# Revit family: Cover_Access_Round-Zurn-Z1469
name_source: partatom
category: Plumbing Fixtures
units: mm (PartAtom-declared; Revit-internal decimal feet)

## family parameters
Cut with Voids When Loaded = No
Host = Face
Maintain Annotation Orientation = No
OmniClass Number = 23.60.30.11.14
OmniClass Title = Pipework Fittings
Part Type = Normal
Room Calculation Point = No
Round Connector Dimension = Use Radius
Shared = No

## types (10) — shared parameters
Assembly Code = D2030100
CW Connection = No
Default Elevation = 20 "
Description = ROUND ACCESS COVER
HW Connection = No
Manufacturer = Zurn Water, LLC
Manufacurer Brand = Zurn
Modified Date = 02/13/2026
Product Documentation Link = https://files.zurn.com
Product Page URL = https://www.zurn.com
Product data url = https://www.bimobject.com
URL = www.zurn.com
Vent Connection = No
WFU = 1
Waste Connection = Yes
zero-valued in all types: CWFU, HWFU

## per-type parameters (varying)
| type | Approx. Weight (Lbs) | Cover Dia (A) | Main Material | Model | Type Comments |
| ZS1469 4 Inch | 1 " | 4 " | Steel – Zurn – Stainless – Polished | ZS1469 | ZS1469-4 Inch Cover |
| ZS1469 5 Inch | 1 " | 5 " | Steel – Zurn – Stainless – Polished | ZS1469 | ZS1469-5 Inch Cover |
| ZS1469 7 Inch | 2 " | 7 " | Steel – Zurn – Stainless – Polished | ZS1469 | ZS1469-7 Inch Cover |
| ZS1469 9 Inch | 3 " | 9 " | Steel – Zurn – Stainless – Polished | ZS1469 | ZS1469-9 Inch Cover |
| ZS1469 11 Inch | 4 " | 11 " | Steel – Zurn – Stainless – Polished | ZS1469 | ZS1469-11 Inch Cover |
| ZAB1469 4 Inch | 1 " | 4 " | Bronze - Zurn - Polished | ZAB1469 | ZAB1469-4 Inch Cover |
| ZAB1469 5 Inch | 1 " | 5 " | Bronze - Zurn - Polished | ZAB1469 | ZAB1469-5 Inch Cover |
| ZAB1469 7 Inch | 2 " | 7 " | Bronze - Zurn - Polished | ZAB1469 | ZAB1469-7 Inch Cover |
| ZAB1469 9 Inch | 3 " | 9 " | Bronze - Zurn - Polished | ZAB1469 | ZAB1469-9 Inch Cover |
| ZAB1469 11 Inch | 4 " | 11 " | Bronze - Zurn - Polished | ZAB1469 | ZAB1469-11 Inch Cover |

## geometry (parser evidence)
native form markers: Sweep x3
no freeform markers — native parametric forms only
